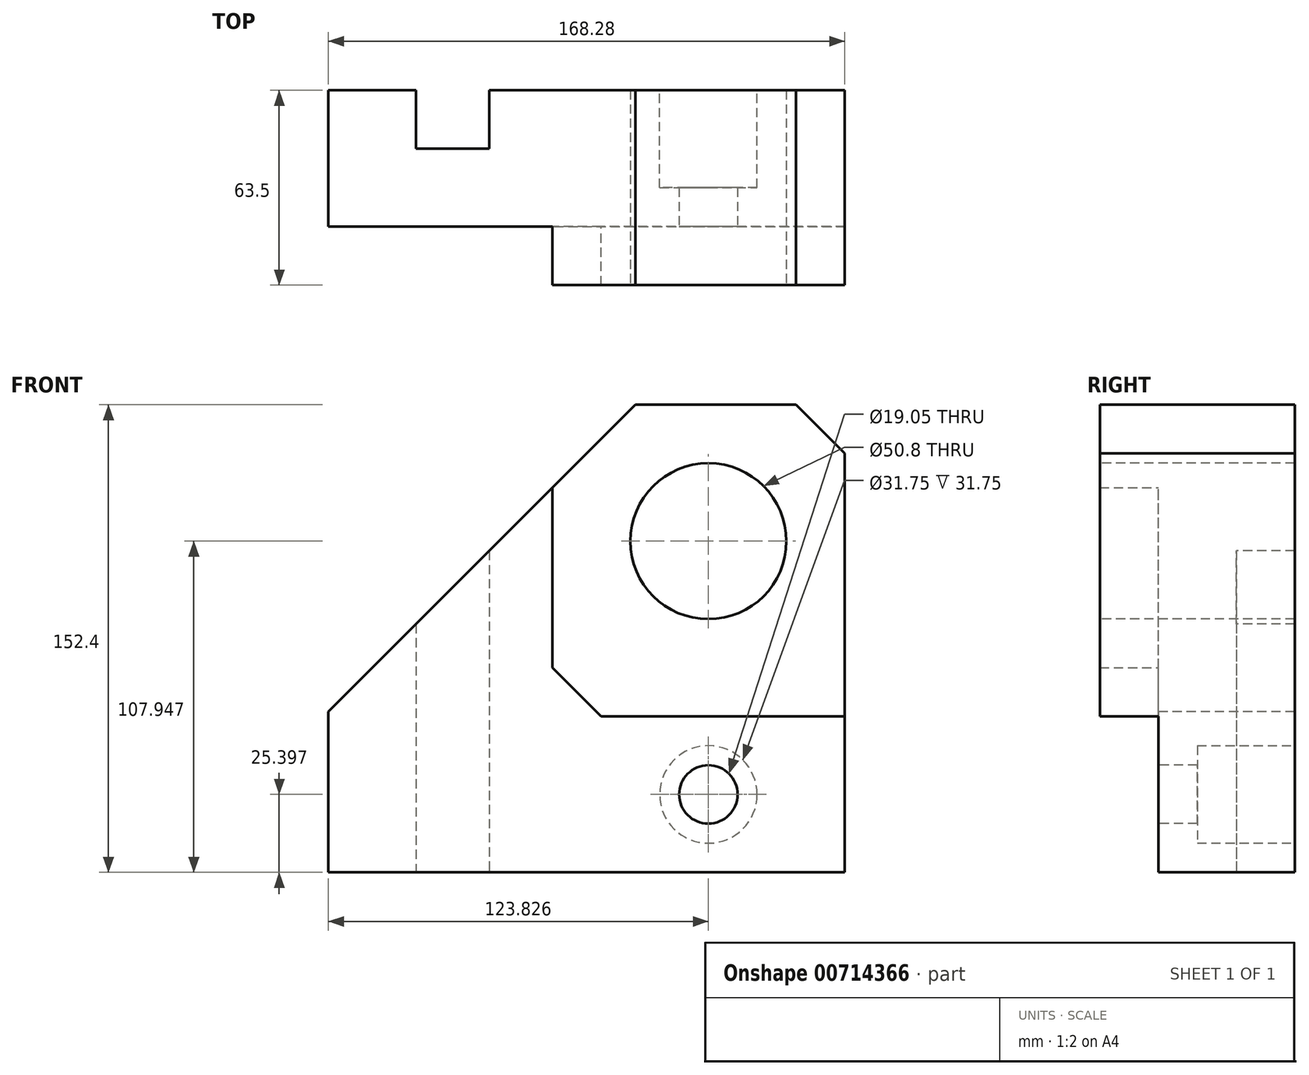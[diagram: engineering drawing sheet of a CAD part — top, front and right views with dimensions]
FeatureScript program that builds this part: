
annotation { "Feature Type Name" : "Feature", "Feature Type Description" : "" }
export const myFeature = defineFeature(function(context is Context, id is Id, definition is map)
    precondition{}
    {
        {
            var Q0;
            Q0=qCreatedBy(makeId("Front.planeOp"),FACE);
            var sketch = newSketch(context, id + "F0", { "sketchPlane" : qUnion([Q0])});
            skLineSegment(sketch, "E0.bottom", {"start": v(-89.98, 52.45) * mm, "end": v(78.3, 52.45) * mm});
            skLineSegment(sketch, "E0.top", {"start": v(-89.98, -99.95) * mm, "end": v(78.3, -99.95) * mm});
            skLineSegment(sketch, "E0.left", {"start": v(-89.98, 52.45) * mm, "end": v(-89.98, -99.95) * mm});
            skLineSegment(sketch, "E0.right", {"start": v(78.3, 52.45) * mm, "end": v(78.3, -99.95) * mm});
            skSolve(sketch);
        }
        {
            var Q0;
            Q0=makeQuery(id+"F0.imprint","IMPRINT",FACE,{"disambiguationData":[TD([[makeQuery(id+"F0.imprint","IMPRINT",EDGE,{"derivedFrom":sQuery(id+"F0.wireOp",EDGE,"E0.bottom")}),-1.0]])]});
            extrude(context, id + "F1", {"entities" : qUnion([Q0]), "depth" : 44.45 * mm, "offsetDistance" : 25.4 * mm});
        }
        {
            var Q0;
            Q0=makeQuery(id+"F1.opExtrude","CAP_FACE",FACE,{"disambiguationData":[OSD([sQuery(id+"F0.wireOp",EDGE,"E0.bottom"),sQuery(id+"F0.wireOp",EDGE,"E0.top"),sQuery(id+"F0.wireOp",EDGE,"E0.left"),sQuery(id+"F0.wireOp",EDGE,"E0.right")])],"isStart":false});
            var sketch = newSketch(context, id + "F2", { "sketchPlane" : qUnion([Q0])});
            skLineSegment(sketch, "E1", {"start": v(-89.98, -47.57) * mm, "end": v(10.03, 52.45) * mm});
            skSolve(sketch);
        }
        {
            var Q0;
            {var subQ0=sQuery(id+"F2.wireOp",EDGE,"E1");Q0=makeQuery(id+"F2.imprint","IMPRINT",FACE,{"disambiguationData":[TD([[makeQuery(id+"F2.imprint","IMPRINT",EDGE,{"derivedFrom":subQ0}),1.0]])]});}
            extrude(context, id + "F3", {"entities" : qUnion([Q0]), "operationType" : NewBodyOperationType.REMOVE, "endBound" : BoundingType.THROUGH_ALL, "oppositeDirection" : true, "depth" : 25.4 * mm, "offsetDistance" : 25.4 * mm});
        }
        {
            var Q0;
            Q0=makeQuery(id+"F1.opExtrude","SWEPT_FACE",FACE,{"disambiguationData":[OSD([sQuery(id+"F0.wireOp",EDGE,"E0.top")])]});
            var sketch = newSketch(context, id + "F4", { "sketchPlane" : qUnion([Q0])});
            skLineSegment(sketch, "E2.bottom", {"start": v(-61.4, 0) * mm, "end": v(-37.6, 0) * mm});
            skLineSegment(sketch, "E2.top", {"start": v(-61.4, 19.05) * mm, "end": v(-37.6, 19.05) * mm});
            skLineSegment(sketch, "E2.left", {"start": v(-61.4, 0) * mm, "end": v(-61.4, 19.05) * mm});
            skLineSegment(sketch, "E2.right", {"start": v(-37.6, 0) * mm, "end": v(-37.6, 19.05) * mm});
            skSolve(sketch);
        }
        {
            var Q0;
            Q0=makeQuery(id+"F4.imprint","IMPRINT",FACE,{"disambiguationData":[TD([[makeQuery(id+"F4.imprint","IMPRINT",EDGE,{"derivedFrom":sQuery(id+"F4.wireOp",EDGE,"E2.bottom")}),1.0]])]});
            extrude(context, id + "F5", {"entities" : qUnion([Q0]), "operationType" : NewBodyOperationType.REMOVE, "endBound" : BoundingType.THROUGH_ALL, "oppositeDirection" : true, "depth" : 25.4 * mm, "offsetDistance" : 25.4 * mm});
        }
        {
            var Q0;
            Q0=makeQuery(id+"F1.opExtrude","CAP_FACE",FACE,{"disambiguationData":[OSD([sQuery(id+"F0.wireOp",EDGE,"E0.bottom"),sQuery(id+"F0.wireOp",EDGE,"E0.top"),sQuery(id+"F0.wireOp",EDGE,"E0.left"),sQuery(id+"F0.wireOp",EDGE,"E0.right")])],"isStart":false});
            var sketch = newSketch(context, id + "F6", { "sketchPlane" : qUnion([Q0])});
            skLineSegment(sketch, "E3", {"start": v(78.3, -49.15) * mm, "end": v(-1.08, -49.15) * mm});
            skLineSegment(sketch, "E4", {"start": v(-1.08, -49.15) * mm, "end": v(-16.95, -33.28) * mm});
            skLineSegment(sketch, "E5", {"start": v(-16.95, -33.28) * mm, "end": v(-16.95, 25.46) * mm});
            skSolve(sketch);
        }
        {
            var Q0;
            {var subQ2=sQuery(id+"F6.wireOp",EDGE,"E3");Q0=makeQuery(id+"F6.imprint","IMPRINT",FACE,{"disambiguationData":[TD([[makeQuery(id+"F6.imprint","IMPRINT",EDGE,{"derivedFrom":subQ2}),-1.0]])]});}
            extrude(context, id + "F7", {"entities" : qUnion([Q0]), "operationType" : NewBodyOperationType.ADD, "depth" : 19.05 * mm, "offsetDistance" : 25.4 * mm});
        }
        {
            var Q0;
            Q0=makeQuery(id+"F7.opExtrude","CAP_FACE",FACE,{"disambiguationData":[OSD([sQuery(id+"F0.wireOp",EDGE,"E0.bottom"),sQuery(id+"F0.wireOp",EDGE,"E0.right"),sQuery(id+"F2.wireOp",EDGE,"E1"),sQuery(id+"F6.wireOp",EDGE,"E3"),sQuery(id+"F6.wireOp",EDGE,"E4"),sQuery(id+"F6.wireOp",EDGE,"E5")])],"isStart":false});
            var sketch = newSketch(context, id + "F8", { "sketchPlane" : qUnion([Q0])});
            skLineSegment(sketch, "E6", {"start": v(62.42, 52.45) * mm, "end": v(78.3, 36.57) * mm});
            skCircle(sketch, "E7", {"center": v(33.85, 8) * mm, "radius": 25.4 * mm});
            skSolve(sketch);
        }
        {
            var Q0;
            Q0=makeQuery(id+"F8.imprint","IMPRINT",FACE,{"disambiguationData":[TD([[makeQuery(id+"F8.imprint","IMPRINT",EDGE,{"derivedFrom":sQuery(id+"F8.wireOp",EDGE,"E7")}),1.0]])]});
            var Q1;
            {var subQ0=sQuery(id+"F8.wireOp",EDGE,"E6");Q1=makeQuery(id+"F8.imprint","IMPRINT",FACE,{"disambiguationData":[TD([[makeQuery(id+"F8.imprint","IMPRINT",EDGE,{"derivedFrom":subQ0}),1.0]])]});}
            extrude(context, id + "F9", {"entities" : qUnion([Q0, Q1]), "operationType" : NewBodyOperationType.REMOVE, "endBound" : BoundingType.THROUGH_ALL, "oppositeDirection" : true, "depth" : 25.4 * mm, "offsetDistance" : 25.4 * mm});
        }
        {
            var Q0;
            Q0=makeQuery(id+"F1.opExtrude","CAP_FACE",FACE,{"disambiguationData":[OSD([sQuery(id+"F0.wireOp",EDGE,"E0.bottom"),sQuery(id+"F0.wireOp",EDGE,"E0.top"),sQuery(id+"F0.wireOp",EDGE,"E0.left"),sQuery(id+"F0.wireOp",EDGE,"E0.right")])],"isStart":false});
            var sketch = newSketch(context, id + "F10", { "sketchPlane" : qUnion([Q0])});
            skCircle(sketch, "E8", {"center": v(33.85, -74.55) * mm, "radius": 9.53 * mm});
            skSolve(sketch);
        }
        {
            var Q0;
            Q0=makeQuery(id+"F10.imprint","IMPRINT",FACE,{"disambiguationData":[TD([[makeQuery(id+"F10.imprint","IMPRINT",EDGE,{"derivedFrom":sQuery(id+"F10.wireOp",EDGE,"E8")}),1.0]])]});
            extrude(context, id + "F11", {"entities" : qUnion([Q0]), "operationType" : NewBodyOperationType.REMOVE, "endBound" : BoundingType.THROUGH_ALL, "oppositeDirection" : true, "depth" : 25.4 * mm, "offsetDistance" : 25.4 * mm});
        }
        {
            var Q0;
            {var subQ0=sQuery(id+"F0.wireOp",EDGE,"E0.right");var subQ1=sQuery(id+"F0.wireOp",EDGE,"E0.top");var subQ2=sQuery(id+"F0.wireOp",EDGE,"E0.bottom");Q0=makeQuery(id+"F5.boolean.opBoolean","SPLIT",FACE,{"disambiguationData":[TD([makeQuery(id+"F1.opExtrude","SWEPT_FACE",FACE,{"disambiguationData":[OSD([subQ2])]})])],"derivedFrom":makeQuery(id+"F1.opExtrude","CAP_FACE",FACE,{"disambiguationData":[OSD([subQ2,subQ1,sQuery(id+"F0.wireOp",EDGE,"E0.left"),subQ0])],"isStart":true})});}
            var sketch = newSketch(context, id + "F12", { "sketchPlane" : qUnion([Q0])});
            skCircle(sketch, "E9", {"center": v(-33.85, -74.55) * mm, "radius": 15.88 * mm});
            skSolve(sketch);
        }
        {
            var Q0;
            Q0=makeQuery(id+"F12.imprint","IMPRINT",FACE,{"disambiguationData":[TD([[makeQuery(id+"F12.imprint","IMPRINT",EDGE,{"derivedFrom":sQuery(id+"F12.wireOp",EDGE,"E9")}),1.0]])]});
            extrude(context, id + "F13", {"entities" : qUnion([Q0]), "operationType" : NewBodyOperationType.REMOVE, "oppositeDirection" : true, "depth" : 31.75 * mm, "offsetDistance" : 25.4 * mm});
        }
    });
